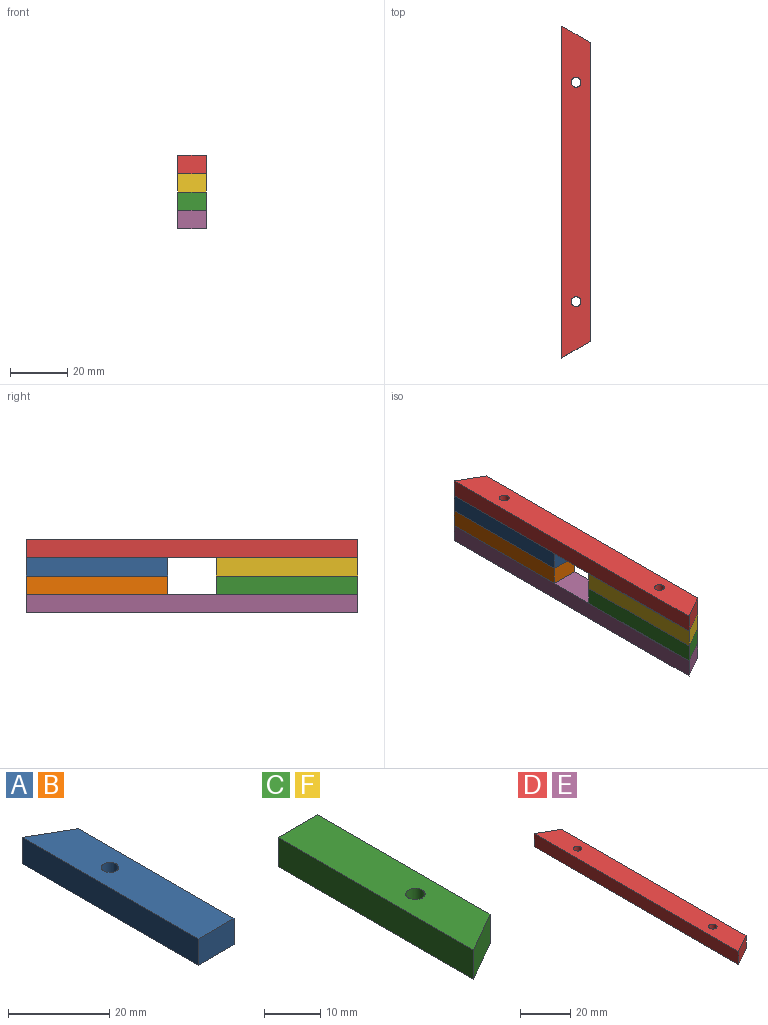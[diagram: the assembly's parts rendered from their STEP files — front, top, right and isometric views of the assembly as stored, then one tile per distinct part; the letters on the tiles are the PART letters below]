
ASSEMBLY  parts=6 mates=10
PART A: 7 faces, bbox 10x49.2x6.4 mm
  f0: plane 49.24x6.35mm, normal (-1,0,0), area 312.6mm2, adj f1,f4,f5,f6
  f1: plane 10x6.35mm, normal (0,-1,0), area 63.5mm2, adj f0,f2,f5,f6
  f2: plane 43.46x6.35mm, normal (1,0,0), area 276mm2, adj f1,f4,f5,f6
  f3: cylinder r=1.73mm len=6.35mm, axis (0,0,-1), area 68.9mm2, adj f5,f6
  f4: plane 10x6.35mm, normal (0.5,0.87,0), area 73.3mm2, adj f0,f2,f5,f6
  f5: plane 49.24x10mm, normal (0,0,1), area 454.1mm2, adj f0,f1,f2,f3,f4
  f6: plane 49.24x10mm, normal (0,0,-1), area 454.1mm2, adj f0,f1,f2,f3,f4
PART B: same geometry as A
PART C: 7 faces, bbox 10x49.2x6.4 mm
  f0: plane 43.46x6.35mm, normal (1,0,0), area 276mm2, adj f1,f4,f5,f6
  f1: plane 10x6.35mm, normal (0,1,0), area 63.5mm2, adj f0,f2,f5,f6
  f2: plane 49.24x6.35mm, normal (-1,0,0), area 312.6mm2, adj f1,f4,f5,f6
  f3: cylinder r=1.73mm len=6.35mm, axis (0,0,-1), area 68.9mm2, adj f5,f6
  f4: plane 10x6.35mm, normal (0.5,-0.87,0), area 73.3mm2, adj f0,f2,f5,f6
  f5: plane 49.24x10mm, normal (0,0,1), area 454.1mm2, adj f0,f1,f2,f3,f4
  f6: plane 49.24x10mm, normal (0,0,-1), area 454.1mm2, adj f0,f1,f2,f3,f4
PART D: 8 faces, bbox 10x115.5x6.4 mm
  f0: plane 10x6.35mm, normal (0.5,-0.87,0), area 73.3mm2, adj f1,f5,f6,f7
  f1: plane 103.92x6.35mm, normal (1,0,0), area 659.9mm2, adj f0,f2,f6,f7
  f2: plane 10x6.35mm, normal (0.5,0.87,0), area 73.3mm2, adj f1,f5,f6,f7
  f3: cylinder r=1.73mm len=6.35mm, axis (0,0,-1), area 68.9mm2, adj f6,f7
  f4: cylinder r=1.73mm len=6.35mm, axis (0,0,-1), area 68.9mm2, adj f6,f7
  f5: plane 115.47x6.35mm, normal (-1,0,0), area 733.2mm2, adj f0,f2,f6,f7
  f6: plane 115.47x10mm, normal (0,0,1), area 1078.2mm2, adj f0,f1,f2,f3,f4,f5
  f7: plane 115.47x10mm, normal (0,0,-1), area 1078.2mm2, adj f0,f1,f2,f3,f4,f5
PART E: same geometry as D
PART F: same geometry as C
PLACE A t=(-93.86,5.84,-49.12)mm
PLACE B t=(-93.86,5.84,-55.47)mm
PLACE C t=(-93.86,5.84,-55.47)mm
PLACE D t=(6.14,5.84,-42.77)mm
PLACE E t=(6.14,5.84,-61.82)mm fixed
PLACE F t=(-93.86,5.84,-49.12)mm
MATE planar C.f2 <-> F.f2  axis (-1,0,0) through (6.14,30.46,-52.3)mm
MATE revolute C.f3 <-> E.f4  axis (0,0,-1) through (11.14,25.43,-55.47)mm
MATE planar B.f0 <-> A.f0  axis (-1,0,0) through (6.14,96.7,-52.3)mm
MATE planar C.f2 <-> E.f5  axis (-1,0,0) through (6.14,55.08,-52.3)mm
MATE planar B.f0 <-> E.f5  axis (-1,0,0) through (6.14,96.7,-52.3)mm
MATE revolute C.f3 <-> F.f3  axis (0,0,1) through (11.14,25.43,-49.12)mm
MATE revolute A.f3 <-> B.f3  axis (0,0,-1) through (11.14,101.73,-49.12)mm
MATE revolute B.f3 <-> E.f3  axis (0,0,-1) through (11.14,101.73,-55.47)mm
MATE revolute F.f3 <-> D.f4  axis (0,0,1) through (11.14,25.43,-42.77)mm
MATE planar D.f5 <-> E.f5  axis (-1,0,0) through (6.14,63.58,-39.6)mm
